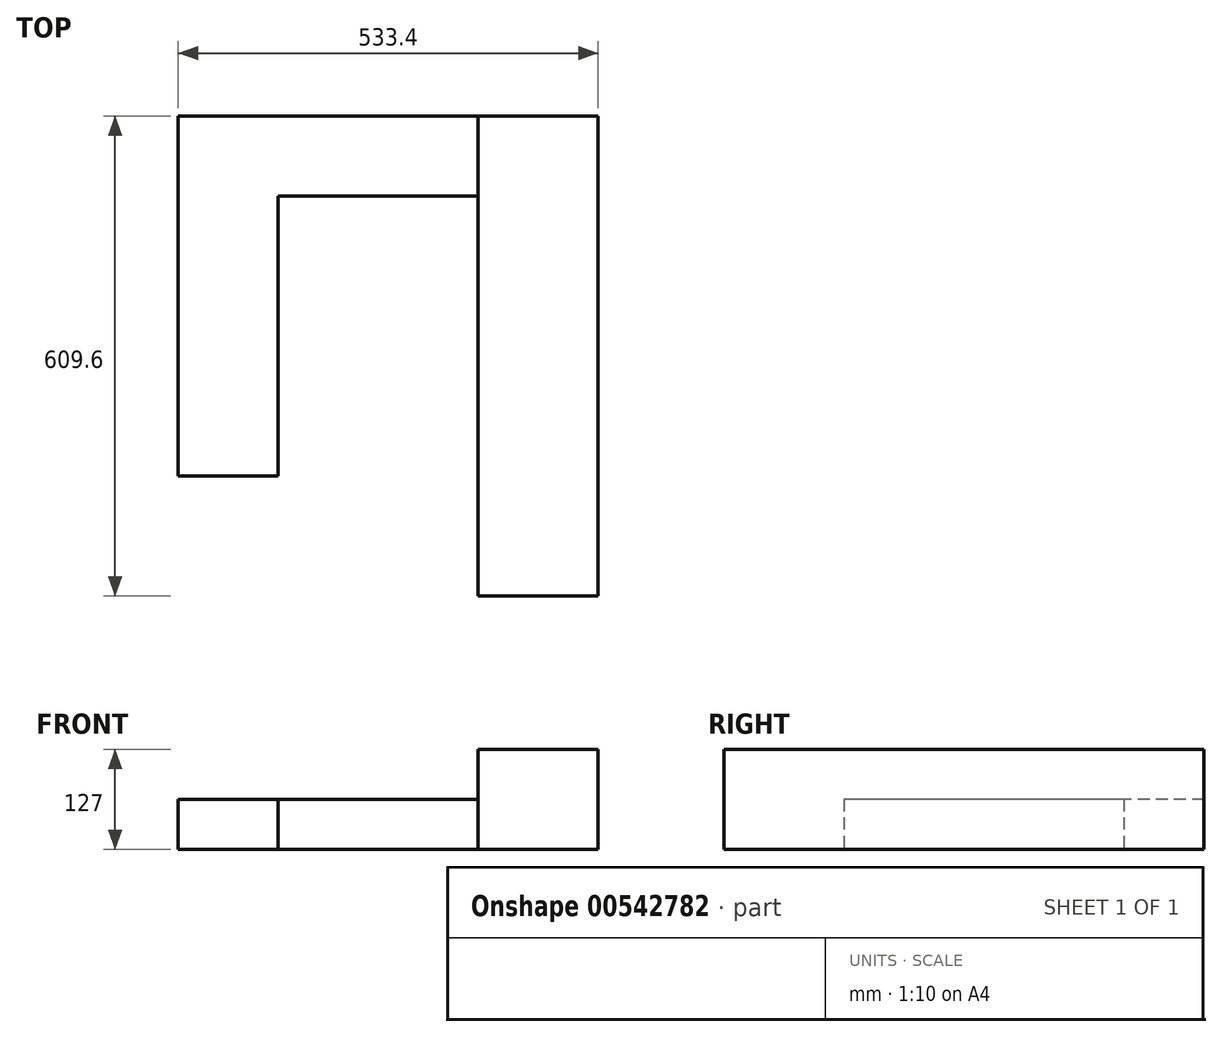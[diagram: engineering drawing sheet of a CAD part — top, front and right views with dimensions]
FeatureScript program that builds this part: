
annotation { "Feature Type Name" : "Feature", "Feature Type Description" : "" }
export const myFeature = defineFeature(function(context is Context, id is Id, definition is map)
    precondition{}
    {
        {
            var Q0;
            Q0=qCreatedBy(makeId("Top.planeOp"),FACE);
            var sketch = newSketch(context, id + "F0", { "sketchPlane" : qUnion([Q0])});
            skLineSegment(sketch, "E0.bottom", {"start": v(111.3, 337.05) * mm, "end": v(263.7, 337.05) * mm});
            skLineSegment(sketch, "E0.top", {"start": v(111.3, -272.55) * mm, "end": v(263.7, -272.55) * mm});
            skLineSegment(sketch, "E0.left", {"start": v(111.3, 337.05) * mm, "end": v(111.3, -272.55) * mm});
            skLineSegment(sketch, "E0.right", {"start": v(263.7, 337.05) * mm, "end": v(263.7, -272.55) * mm});
            skLineSegment(sketch, "E1.bottom", {"start": v(111.3, 337.05) * mm, "end": v(-142.7, 337.05) * mm});
            skLineSegment(sketch, "E1.top", {"start": v(111.3, 235.45) * mm, "end": v(-142.7, 235.45) * mm});
            skLineSegment(sketch, "E1.left", {"start": v(111.3, 337.05) * mm, "end": v(111.3, 235.45) * mm});
            skLineSegment(sketch, "E1.right", {"start": v(-142.7, 337.05) * mm, "end": v(-142.7, 235.45) * mm});
            skLineSegment(sketch, "E2.bottom", {"start": v(-142.7, 337.05) * mm, "end": v(-269.7, 337.05) * mm});
            skLineSegment(sketch, "E2.top", {"start": v(-142.7, -120.15) * mm, "end": v(-269.7, -120.15) * mm});
            skLineSegment(sketch, "E2.left", {"start": v(-142.7, 337.05) * mm, "end": v(-142.7, -120.15) * mm});
            skLineSegment(sketch, "E2.right", {"start": v(-269.7, 337.05) * mm, "end": v(-269.7, -120.15) * mm});
            skSolve(sketch);
        }
        {
            var Q0;
            {var subQ3=sQuery(id+"F0.wireOp",EDGE,"E2.bottom");Q0=makeQuery(id+"F0.imprint","IMPRINT",FACE,{"disambiguationData":[TD([[makeQuery(id+"F0.imprint","IMPRINT",EDGE,{"derivedFrom":subQ3}),1.0]])]});}
            var Q1;
            {var subQ0=sQuery(id+"F0.wireOp",EDGE,"E1.bottom");Q1=makeQuery(id+"F0.imprint","IMPRINT",FACE,{"disambiguationData":[TD([[makeQuery(id+"F0.imprint","IMPRINT",EDGE,{"derivedFrom":subQ0}),1.0]])]});}
            extrude(context, id + "F1", {"entities" : qUnion([Q0, Q1]), "depth" : 63.5 * mm, "offsetDistance" : 25.4 * mm});
        }
        {
            var Q0;
            Q0=makeQuery(id+"F0.imprint","IMPRINT",FACE,{"disambiguationData":[TD([[makeQuery(id+"F0.imprint","IMPRINT",EDGE,{"derivedFrom":sQuery(id+"F0.wireOp",EDGE,"E0.bottom")}),-1.0]])]});
            extrude(context, id + "F2", {"entities" : qUnion([Q0]), "operationType" : NewBodyOperationType.ADD, "depth" : 127 * mm, "offsetDistance" : 25.4 * mm});
        }
    });
